# Revit family: GRAS_HW-25W-SK-20-30
name_source: partatom
category: Osprzęt hydrauliczny
revit_build: Autodesk Revit 2018 (Build: 20190510_1515(x64)
units: mm (PartAtom-declared; Revit-internal decimal feet)

## family parameters
Obiekt nadrzędny = Powierzchnia
Punkt obliczania pomieszczeń = Nie
Tnij formami wycięć po wczytaniu = Nie
Typ części = Normalny
Współdzielony = Nie
Wymiar okrągłego złącza = Użyj średnicy

## types (2) — shared parameters
Cabinet_Depth = 700 mm  [stored 2.29659 ft]
Cabinet_Width = 260 mm  [stored 0.853018 ft]
D1 = 100 mm  [stored 0.328084 ft]
DN = 25 mm  [stored 0.082021 ft]
Flow = 60.0 L/s
Hole_Depth = 710 mm
Hole_Width = 280 mm  [stored 0.918635 ft]
K_factor = 42
Producent = GRAS PPPH
URL = http://www.gras.pl
W1 = 130 mm  [stored 0.426509 ft]
zero-valued in all types: Domyślna rzędna

## per-type parameters (varying)
| type | Cabinet_Height | Cabinet_Material | Hole_Height | Model | Opis |
| HW-25W-SK-20-30, RAL9010 | 840 mm  [stored 2.75591 ft] | DC01, RAL9010 | 860 mm  [stored 2.82152 ft] | HW-25W-SK-20/30, RAL9010 |  |
| HW-25W-SK-20-30, RAL3000 | 1040 mm  [stored 3.41207 ft] | DC01, RAL3000 | 1060 mm | HW-25W-SK-20/30, RAL3000 | http://gras.pl |

note: [stored X ft] marks values corroborated as IEEE doubles in the binary element streams (Revit-internal decimal feet)

## geometry (parser evidence)
native form markers: Blend x8
no freeform markers — native parametric forms only
